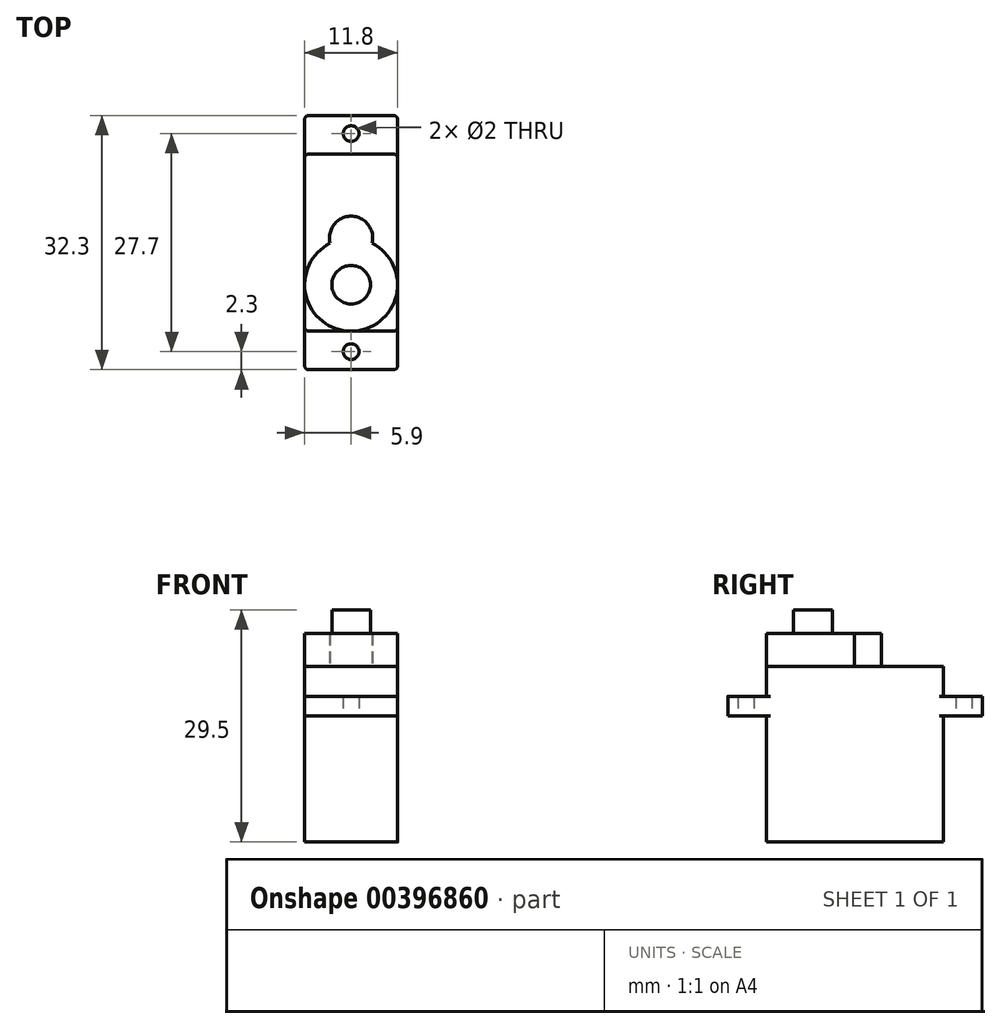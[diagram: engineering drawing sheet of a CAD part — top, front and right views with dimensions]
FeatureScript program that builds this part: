
annotation { "Feature Type Name" : "Feature", "Feature Type Description" : "" }
export const myFeature = defineFeature(function(context is Context, id is Id, definition is map)
    precondition{}
    {
        {
            var Q0;
            Q0=qCreatedBy(makeId("Top.planeOp"),FACE);
            var sketch = newSketch(context, id + "F0", { "sketchPlane" : qUnion([Q0])});
            skLineSegment(sketch, "E0.bottom", {"start": v(0, 0) * mm, "end": v(11.8, 0) * mm});
            skLineSegment(sketch, "E0.top", {"start": v(0, 22.5) * mm, "end": v(11.8, 22.5) * mm});
            skLineSegment(sketch, "E0.left", {"start": v(0, 0) * mm, "end": v(0, 22.5) * mm});
            skLineSegment(sketch, "E0.right", {"start": v(11.8, 0) * mm, "end": v(11.8, 22.5) * mm});
            skSolve(sketch);
        }
        {
            var Q0;
            Q0=makeQuery(id+"F0.imprint","IMPRINT",FACE,{"disambiguationData":[TD([[makeQuery(id+"F0.imprint","IMPRINT",EDGE,{"derivedFrom":sQuery(id+"F0.wireOp",EDGE,"E0.bottom")}),1.0]])]});
            extrude(context, id + "F1", {"entities" : qUnion([Q0]), "depth" : 22.3 * mm});
        }
        {
            var Q0;
            Q0=qCreatedBy(makeId("Top.planeOp"),FACE);
            cPlane(context, id + "F2", {"entities" : qUnion([Q0]), "cplaneType" : CPlaneType.OFFSET, "offset" : 16 * mm, "width" : 150 * mm, "height" : 150 * mm});
        }
        {
            var Q0;
            Q0=qCreatedBy(id+"F2.planeOp",FACE);
            var sketch = newSketch(context, id + "F3", { "sketchPlane" : qUnion([Q0])});
            skLineSegment(sketch, "E1.bottom", {"start": v(0, 27.4) * mm, "end": v(11.8, 27.4) * mm});
            skLineSegment(sketch, "E1.top", {"start": v(0, -4.9) * mm, "end": v(11.8, -4.9) * mm});
            skLineSegment(sketch, "E1.left", {"start": v(0, 27.4) * mm, "end": v(0, -4.9) * mm});
            skLineSegment(sketch, "E1.right", {"start": v(11.8, 27.4) * mm, "end": v(11.8, -4.9) * mm});
            skCircle(sketch, "E2", {"center": v(5.9, -2.6) * mm, "radius": 1 * mm});
            skPoint(sketch, "E2.centerSnap0", {"position": v(5.9, -4.9) * mm});
            skCircle(sketch, "E3", {"center": v(5.9, 25.1) * mm, "radius": 1 * mm});
            skPoint(sketch, "E3.centerSnap0", {"position": v(5.9, 27.4) * mm});
            skLineSegment(sketch, "E4", {"start": v(5.9, 25.1) * mm, "end": v(5.9, -2.6) * mm});
            skLineSegment(sketch, "E5", {"start": v(5.9, 11.25) * mm, "end": v(0, 11.25) * mm});
            skSolve(sketch);
        }
        {
            var Q0;
            Q0 = qSketchRegion(id + "F3", true);
            extrude(context, id + "F4", {"entities" : qUnion([Q0]), "operationType" : NewBodyOperationType.ADD, "depth" : 2.5 * mm});
        }
        {
            var Q0;
            Q0=makeQuery(id+"F1.opExtrude","CAP_FACE",FACE,{"disambiguationData":[OSD([sQuery(id+"F0.wireOp",EDGE,"E0.bottom"),sQuery(id+"F0.wireOp",EDGE,"E0.top"),sQuery(id+"F0.wireOp",EDGE,"E0.left"),sQuery(id+"F0.wireOp",EDGE,"E0.right")])],"isStart":false});
            var sketch = newSketch(context, id + "F5", { "sketchPlane" : qUnion([Q0])});
            skCircle(sketch, "E6", {"center": v(5.9, 5.9) * mm, "radius": 5.9 * mm});
            skPoint(sketch, "E6.centerSnap0", {"position": v(5.9, 0) * mm});
            skCircle(sketch, "E7", {"center": v(5.9, 11.85) * mm, "radius": 2.75 * mm});
            skSolve(sketch);
        }
        {
            var Q0;
            Q0 = qSketchRegion(id + "F5", true);
            extrude(context, id + "F6", {"entities" : qUnion([Q0]), "operationType" : NewBodyOperationType.ADD, "depth" : 4.2 * mm});
        }
        {
            var Q0;
            Q0=makeQuery(id+"F6.opExtrude","CAP_FACE",FACE,{"disambiguationData":[OSD([sQuery(id+"F5.wireOp",EDGE,"E6"),sQuery(id+"F5.wireOp",EDGE,"E7")])],"isStart":false});
            var sketch = newSketch(context, id + "F7", { "sketchPlane" : qUnion([Q0])});
            skCircle(sketch, "E8", {"center": v(5.9, 5.9) * mm, "radius": 2.45 * mm});
            skSolve(sketch);
        }
        {
            var Q0;
            Q0=makeQuery(id+"F7.imprint","IMPRINT",FACE,{"disambiguationData":[TD([[makeQuery(id+"F7.imprint","IMPRINT",EDGE,{"derivedFrom":sQuery(id+"F7.wireOp",EDGE,"E8")}),1.0]])]});
            extrude(context, id + "F8", {"entities" : qUnion([Q0]), "operationType" : NewBodyOperationType.ADD, "depth" : 3 * mm});
        }
        {
            var Q0;
            {var subQ1=sQuery(id+"F0.wireOp",EDGE,"E0.right");var subQ2=sQuery(id+"F0.wireOp",EDGE,"E0.bottom");Q0=makeQuery(id+"F4.boolean.opBoolean","SPLIT",EDGE,{"disambiguationData":[TD([makeQuery(id+"F1.opExtrude","CAP_FACE",FACE,{"disambiguationData":[OSD([subQ2,sQuery(id+"F0.wireOp",EDGE,"E0.top"),sQuery(id+"F0.wireOp",EDGE,"E0.left"),subQ1])],"isStart":true})])],"derivedFrom":makeQuery(id+"F1.opExtrude","SWEPT_EDGE",EDGE,{"disambiguationData":[OSD([subQ2,subQ1])]})});}
            var Q1;
            {var subQ1=sQuery(id+"F0.wireOp",EDGE,"E0.right");var subQ2=sQuery(id+"F0.wireOp",EDGE,"E0.bottom");Q1=makeQuery(id+"F4.boolean.opBoolean","SPLIT",EDGE,{"disambiguationData":[TD([makeQuery(id+"F1.opExtrude","CAP_FACE",FACE,{"disambiguationData":[OSD([subQ2,sQuery(id+"F0.wireOp",EDGE,"E0.top"),sQuery(id+"F0.wireOp",EDGE,"E0.left"),subQ1])],"isStart":false})])],"derivedFrom":makeQuery(id+"F1.opExtrude","SWEPT_EDGE",EDGE,{"disambiguationData":[OSD([subQ2,subQ1])]})});}
            var Q2;
            {var subQ1=sQuery(id+"F0.wireOp",EDGE,"E0.left");var subQ2=sQuery(id+"F0.wireOp",EDGE,"E0.bottom");Q2=makeQuery(id+"F4.boolean.opBoolean","SPLIT",EDGE,{"disambiguationData":[TD([makeQuery(id+"F1.opExtrude","CAP_FACE",FACE,{"disambiguationData":[OSD([subQ2,sQuery(id+"F0.wireOp",EDGE,"E0.top"),subQ1,sQuery(id+"F0.wireOp",EDGE,"E0.right")])],"isStart":true})])],"derivedFrom":makeQuery(id+"F1.opExtrude","SWEPT_EDGE",EDGE,{"disambiguationData":[OSD([subQ2,subQ1])]})});}
            var Q3;
            {var subQ1=sQuery(id+"F0.wireOp",EDGE,"E0.left");var subQ2=sQuery(id+"F0.wireOp",EDGE,"E0.bottom");Q3=makeQuery(id+"F4.boolean.opBoolean","SPLIT",EDGE,{"disambiguationData":[TD([makeQuery(id+"F1.opExtrude","CAP_FACE",FACE,{"disambiguationData":[OSD([subQ2,sQuery(id+"F0.wireOp",EDGE,"E0.top"),subQ1,sQuery(id+"F0.wireOp",EDGE,"E0.right")])],"isStart":false})])],"derivedFrom":makeQuery(id+"F1.opExtrude","SWEPT_EDGE",EDGE,{"disambiguationData":[OSD([subQ2,subQ1])]})});}
            var Q4;
            {var subQ0=sQuery(id+"F0.wireOp",EDGE,"E0.left");var subQ2=sQuery(id+"F0.wireOp",EDGE,"E0.top");Q4=makeQuery(id+"F4.boolean.opBoolean","SPLIT",EDGE,{"disambiguationData":[TD([makeQuery(id+"F1.opExtrude","CAP_FACE",FACE,{"disambiguationData":[OSD([sQuery(id+"F0.wireOp",EDGE,"E0.bottom"),subQ2,subQ0,sQuery(id+"F0.wireOp",EDGE,"E0.right")])],"isStart":false})])],"derivedFrom":makeQuery(id+"F1.opExtrude","SWEPT_EDGE",EDGE,{"disambiguationData":[OSD([subQ2,subQ0])]})});}
            var Q5;
            {var subQ1=sQuery(id+"F0.wireOp",EDGE,"E0.top");var subQ2=sQuery(id+"F0.wireOp",EDGE,"E0.left");Q5=makeQuery(id+"F4.boolean.opBoolean","SPLIT",EDGE,{"disambiguationData":[TD([makeQuery(id+"F1.opExtrude","CAP_FACE",FACE,{"disambiguationData":[OSD([sQuery(id+"F0.wireOp",EDGE,"E0.bottom"),subQ1,subQ2,sQuery(id+"F0.wireOp",EDGE,"E0.right")])],"isStart":true})])],"derivedFrom":makeQuery(id+"F1.opExtrude","SWEPT_EDGE",EDGE,{"disambiguationData":[OSD([subQ1,subQ2])]})});}
            var Q6;
            {var subQ1=sQuery(id+"F0.wireOp",EDGE,"E0.top");var subQ2=sQuery(id+"F0.wireOp",EDGE,"E0.right");Q6=makeQuery(id+"F4.boolean.opBoolean","SPLIT",EDGE,{"disambiguationData":[TD([makeQuery(id+"F1.opExtrude","CAP_FACE",FACE,{"disambiguationData":[OSD([sQuery(id+"F0.wireOp",EDGE,"E0.bottom"),subQ1,sQuery(id+"F0.wireOp",EDGE,"E0.left"),subQ2])],"isStart":true})])],"derivedFrom":makeQuery(id+"F1.opExtrude","SWEPT_EDGE",EDGE,{"disambiguationData":[OSD([subQ1,subQ2])]})});}
            var Q7;
            {var subQ0=sQuery(id+"F0.wireOp",EDGE,"E0.right");var subQ2=sQuery(id+"F0.wireOp",EDGE,"E0.top");Q7=makeQuery(id+"F4.boolean.opBoolean","SPLIT",EDGE,{"disambiguationData":[TD([makeQuery(id+"F1.opExtrude","CAP_FACE",FACE,{"disambiguationData":[OSD([sQuery(id+"F0.wireOp",EDGE,"E0.bottom"),subQ2,sQuery(id+"F0.wireOp",EDGE,"E0.left"),subQ0])],"isStart":false})])],"derivedFrom":makeQuery(id+"F1.opExtrude","SWEPT_EDGE",EDGE,{"disambiguationData":[OSD([subQ2,subQ0])]})});}
            var Q8;
            Q8=makeQuery(id+"F4.opExtrude","SWEPT_EDGE",EDGE,{"disambiguationData":[OSD([sQuery(id+"F3.wireOp",EDGE,"E1.top"),sQuery(id+"F3.wireOp",EDGE,"E1.left")])]});
            var Q9;
            Q9=makeQuery(id+"F4.opExtrude","SWEPT_EDGE",EDGE,{"disambiguationData":[OSD([sQuery(id+"F3.wireOp",EDGE,"E1.top"),sQuery(id+"F3.wireOp",EDGE,"E1.right")])]});
            var Q10;
            Q10=makeQuery(id+"F4.opExtrude","SWEPT_EDGE",EDGE,{"disambiguationData":[OSD([sQuery(id+"F3.wireOp",EDGE,"E1.bottom"),sQuery(id+"F3.wireOp",EDGE,"E1.right")])]});
            var Q11;
            Q11=makeQuery(id+"F4.opExtrude","SWEPT_EDGE",EDGE,{"disambiguationData":[OSD([sQuery(id+"F3.wireOp",EDGE,"E1.bottom"),sQuery(id+"F3.wireOp",EDGE,"E1.left")])]});
            fillet(context, id + "F9", {"entities" : qUnion([Q0, Q1, Q2, Q3, Q4, Q5, Q6, Q7, Q8, Q9, Q10, Q11]), "radius" : .5 * mm, "tangentPropagation" : true, "allowEdgeOverflow" : false});
        }
    });
